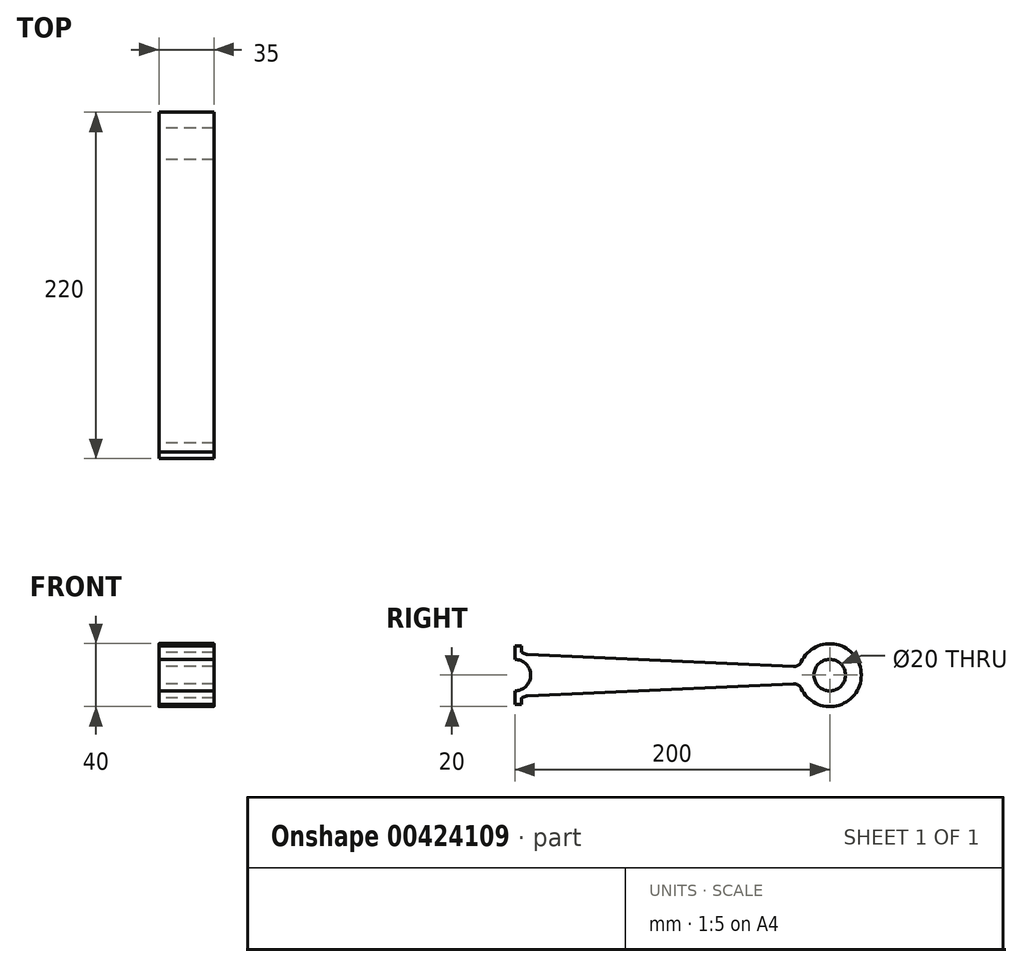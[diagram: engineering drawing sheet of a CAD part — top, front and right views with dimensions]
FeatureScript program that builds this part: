
annotation { "Feature Type Name" : "Feature", "Feature Type Description" : "" }
export const myFeature = defineFeature(function(context is Context, id is Id, definition is map)
    precondition{}
    {
        {
            var Q0;
            Q0=qCreatedBy(makeId("Right.planeOp"),FACE);
            var sketch = newSketch(context, id + "F0", { "sketchPlane" : qUnion([Q0])});
            skCircle(sketch, "E0", {"center": v(200, 0) * mm, "radius": 10 * mm});
            skArc(sketch, "E1", {"start": v(180.72, -5.32) * mm, "mid": v(220, 0) * mm, "end": v(180.72, 5.32) * mm});
            skArc(sketch, "E2", {"start": v(0, 10) * mm, "mid": v(10, 0) * mm, "end": v(0, -10) * mm});
            skLineSegment(sketch, "E3", {"start": v(0, 10) * mm, "end": v(0, 14.35) * mm});
            skLineSegment(sketch, "E4", {"start": v(0, 14.35) * mm, "end": v(4.35, 14.35) * mm, "construction": true});
            skLineSegment(sketch, "E5", {"start": v(0, -10) * mm, "end": v(0, -14.35) * mm});
            skLineSegment(sketch, "E6", {"start": v(0, -14.35) * mm, "end": v(4.35, -14.35) * mm, "construction": true});
            skArc(sketch, "E7", {"start": v(4.35, 14.35) * mm, "mid": v(5.76, 13.85) * mm, "end": v(7.1, 13.21) * mm});
            skLineSegment(sketch, "E8", {"start": v(180.72, -5.32) * mm, "end": v(7.1, -13.21) * mm});
            skLineSegment(sketch, "E9", {"start": v(180.72, 5.32) * mm, "end": v(7.1, 13.21) * mm});
            skArc(sketch, "E10", {"start": v(7.1, 13.21) * mm, "mid": v(15, 0) * mm, "end": v(7.1, -13.21) * mm, "construction": true});
            skArc(sketch, "E11", {"start": v(7.1, -13.21) * mm, "mid": v(5.76, -13.85) * mm, "end": v(4.35, -14.35) * mm});
            skLineSegment(sketch, "E12", {"start": v(0, 14.35) * mm, "end": v(0, 18.7) * mm});
            skLineSegment(sketch, "E13", {"start": v(0, 18.7) * mm, "end": v(4.35, 18.7) * mm});
            skLineSegment(sketch, "E14", {"start": v(4.35, 18.7) * mm, "end": v(4.35, 14.35) * mm});
            skLineSegment(sketch, "E15", {"start": v(0, -14.35) * mm, "end": v(0, -18.7) * mm});
            skLineSegment(sketch, "E16", {"start": v(0, -18.7) * mm, "end": v(4.35, -18.7) * mm});
            skLineSegment(sketch, "E17", {"start": v(4.35, -18.7) * mm, "end": v(4.35, -14.35) * mm});
            skLineSegment(sketch, "E18", {"start": v(180.72, 5.32) * mm, "end": v(200, 0) * mm, "construction": true});
            skLineSegment(sketch, "E19", {"start": v(180.72, -5.32) * mm, "end": v(200, 0) * mm, "construction": true});
            skSolve(sketch);
        }
        {
            var Q0;
            Q0=makeQuery(id+"F0.imprint","IMPRINT",FACE,{"disambiguationData":[TD([[makeQuery(id+"F0.imprint","IMPRINT",EDGE,{"derivedFrom":sQuery(id+"F0.wireOp",EDGE,"E0")}),-1.0]])]});
            extrude(context, id + "F1", {"entities" : qUnion([Q0]), "depth" : 35 * mm});
        }
        {
            var Q0;
            Q0=makeQuery(id+"F1.opExtrude","SWEPT_EDGE",EDGE,{"disambiguationData":[OSD([sQuery(id+"F0.wireOp",EDGE,"E7"),sQuery(id+"F0.wireOp",EDGE,"E9")])]});
            var Q1;
            Q1=makeQuery(id+"F1.opExtrude","SWEPT_EDGE",EDGE,{"disambiguationData":[OSD([sQuery(id+"F0.wireOp",EDGE,"E1"),sQuery(id+"F0.wireOp",EDGE,"E9")])]});
            var Q2;
            Q2=makeQuery(id+"F1.opExtrude","SWEPT_EDGE",EDGE,{"disambiguationData":[OSD([sQuery(id+"F0.wireOp",EDGE,"E1"),sQuery(id+"F0.wireOp",EDGE,"E8")])]});
            var Q3;
            Q3=makeQuery(id+"F1.opExtrude","SWEPT_EDGE",EDGE,{"disambiguationData":[OSD([sQuery(id+"F0.wireOp",EDGE,"E8"),sQuery(id+"F0.wireOp",EDGE,"E11")])]});
            var Q4;
            Q4=makeQuery(id+"F1.opExtrude","SWEPT_EDGE",EDGE,{"disambiguationData":[OSD([sQuery(id+"F0.wireOp",EDGE,"Z1ShSs9c-3PjH-wm5z-G5CJ-mZH7dfjtzP4b"),sQuery(id+"F0.wireOp",EDGE,"o2Rf1S6B-RYFK-5itG-AvDe-jTI4IefRWSlg")])]});
            var Q5;
            Q5=makeQuery(id+"F1.opExtrude","SWEPT_EDGE",EDGE,{"disambiguationData":[OSD([sQuery(id+"F0.wireOp",EDGE,"SzBAzzOP-nz3Q-1jLg-4rDf-IJEnfVqHWDoU"),sQuery(id+"F0.wireOp",EDGE,"o2Rf1S6B-RYFK-5itG-AvDe-jTI4IefRWSlg")])]});
            var Q6;
            Q6=makeQuery(id+"F1.opExtrude","SWEPT_EDGE",EDGE,{"disambiguationData":[OSD([sQuery(id+"F0.wireOp",EDGE,"UylnSdvG-Nf4u-32rj-TI1D-3ZCpgkoLIpsI"),sQuery(id+"F0.wireOp",EDGE,"Z1ShSs9c-3PjH-wm5z-G5CJ-mZH7dfjtzP4b")])]});
            var Q7;
            Q7=makeQuery(id+"F1.opExtrude","SWEPT_EDGE",EDGE,{"disambiguationData":[OSD([sQuery(id+"F0.wireOp",EDGE,"UylnSdvG-Nf4u-32rj-TI1D-3ZCpgkoLIpsI"),sQuery(id+"F0.wireOp",EDGE,"SzBAzzOP-nz3Q-1jLg-4rDf-IJEnfVqHWDoU")])]});
            fillet(context, id + "F2", {"entities" : qUnion([Q0, Q1, Q2, Q3, Q4, Q5, Q6, Q7]), "radius" : 5 * mm, "tangentPropagation" : true, "allowEdgeOverflow" : false});
        }
    });
